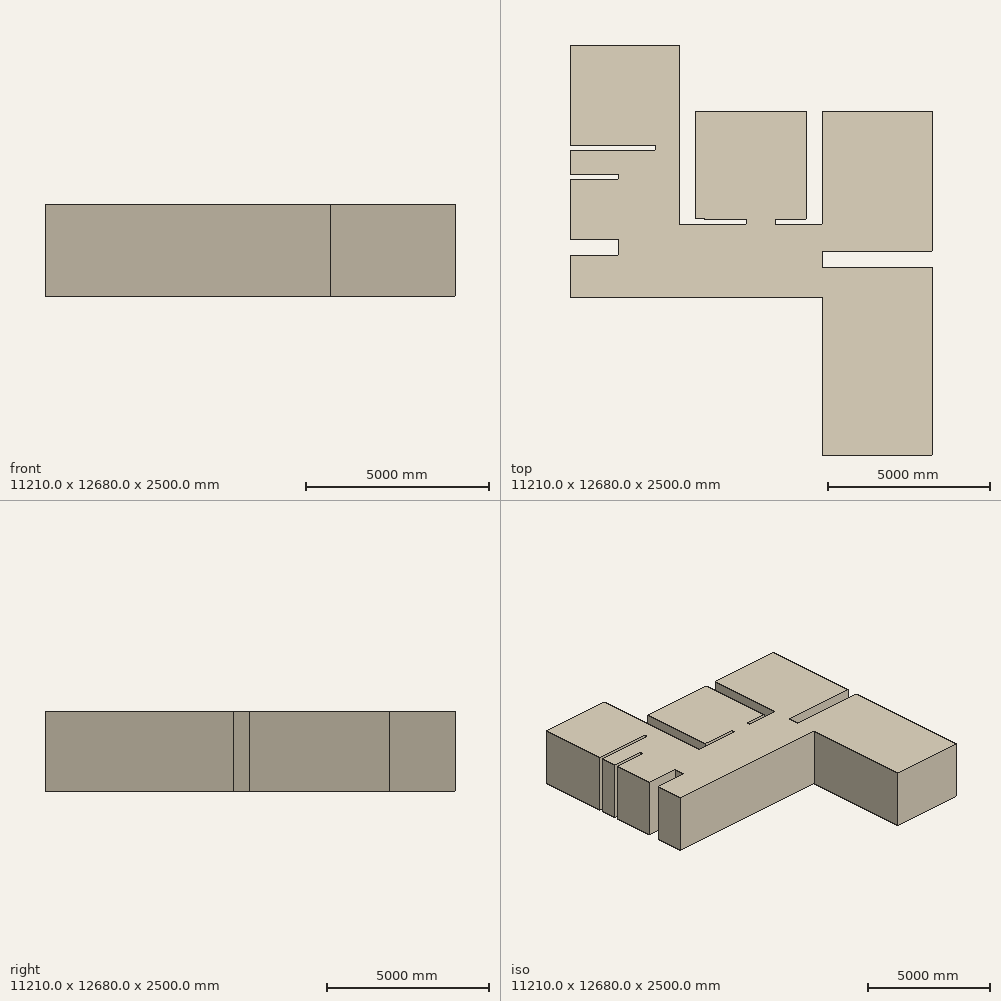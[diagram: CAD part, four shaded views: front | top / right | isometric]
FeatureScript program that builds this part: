
annotation { "Feature Type Name" : "Feature", "Feature Type Description" : "" }
export const myFeature = defineFeature(function(context is Context, id is Id, definition is map)
    precondition{}
    {
        {
            var Q0;
            Q0=qCreatedBy(makeId("Top.planeOp"),FACE);
            var sketch = newSketch(context, id + "F0", { "sketchPlane" : qUnion([Q0])});
            skLineSegment(sketch, "E0", {"start": v(0, 0) * mm, "end": v(-3380, 0) * mm});
            skLineSegment(sketch, "E1", {"start": v(-3380, 0) * mm, "end": v(-3380, -3100) * mm});
            skLineSegment(sketch, "E2", {"start": v(-3380, -3100) * mm, "end": v(-738.11, -3100) * mm});
            skLineSegment(sketch, "E3", {"start": v(-3380, -3980) * mm, "end": v(-1880, -3980) * mm});
            skLineSegment(sketch, "E4", {"start": v(-1880, -3980) * mm, "end": v(-1880, -4130) * mm});
            skLineSegment(sketch, "E5", {"start": v(-1880, -4130) * mm, "end": v(-3380, -4130) * mm});
            skLineSegment(sketch, "E6", {"start": v(-3380, -4130) * mm, "end": v(-3380, -6000) * mm});
            skLineSegment(sketch, "E7", {"start": v(-3380, -7790) * mm, "end": v(4420, -7790) * mm});
            skLineSegment(sketch, "E8", {"start": v(4420, -7790) * mm, "end": v(4420, -12680) * mm});
            skLineSegment(sketch, "E9", {"start": v(4420, -12680) * mm, "end": v(7830, -12680) * mm});
            skLineSegment(sketch, "E10", {"start": v(4420, -2030) * mm, "end": v(4420, -5380) * mm});
            skLineSegment(sketch, "E11", {"start": v(3920, -5380) * mm, "end": v(3920, -2030) * mm});
            skLineSegment(sketch, "E12", {"start": v(0, -2393) * mm, "end": v(0, 0) * mm});
            skLineSegment(sketch, "E13", {"start": v(500, -2030) * mm, "end": v(3920, -2030) * mm});
            skLineSegment(sketch, "E14", {"start": v(7830, -6370) * mm, "end": v(4420, -6370) * mm});
            skLineSegment(sketch, "E15", {"start": v(4420, -6370) * mm, "end": v(4420, -6870) * mm});
            skLineSegment(sketch, "E16", {"start": v(4420, -6870) * mm, "end": v(7830, -6870) * mm});
            skLineSegment(sketch, "E17", {"start": v(7830, -6870) * mm, "end": v(7830, -12680) * mm});
            skLineSegment(sketch, "E18", {"start": v(-738.11, -3100) * mm, "end": v(-738.11, -3250) * mm});
            skLineSegment(sketch, "E19", {"start": v(-738.11, -3250) * mm, "end": v(-3380, -3250) * mm});
            skLineSegment(sketch, "E20", {"start": v(-3380, -3250) * mm, "end": v(-3380, -3980) * mm});
            skLineSegment(sketch, "E21", {"start": v(-3380, -6000) * mm, "end": v(-1880, -6000) * mm});
            skLineSegment(sketch, "E22", {"start": v(-1880, -6000) * mm, "end": v(-1880, -6500) * mm});
            skLineSegment(sketch, "E23", {"start": v(-1880, -6500) * mm, "end": v(-3380, -6500) * mm});
            skLineSegment(sketch, "E24", {"start": v(-3380, -6500) * mm, "end": v(-3380, -7790) * mm});
            skLineSegment(sketch, "E25", {"start": v(0, -2393) * mm, "end": v(0, -5380) * mm});
            skLineSegment(sketch, "E26", {"start": v(4420, -2030) * mm, "end": v(7830, -2030) * mm});
            skLineSegment(sketch, "E27", {"start": v(7830, -2030) * mm, "end": v(7830, -6370) * mm});
            skLineSegment(sketch, "E28", {"start": v(0, -5380) * mm, "end": v(0, -5530) * mm});
            skLineSegment(sketch, "E29", {"start": v(0, -5530) * mm, "end": v(2066.42, -5530) * mm});
            skLineSegment(sketch, "E30", {"start": v(2066.42, -5530) * mm, "end": v(2055.7, -5380) * mm});
            skLineSegment(sketch, "E31", {"start": v(500, -2030) * mm, "end": v(500, -5362.31) * mm});
            skLineSegment(sketch, "E32", {"start": v(500, -5362.31) * mm, "end": v(2055.7, -5380) * mm});
            skLineSegment(sketch, "E33", {"start": v(3920, -5530) * mm, "end": v(2966.42, -5530) * mm});
            skLineSegment(sketch, "E34", {"start": v(2966.42, -5530) * mm, "end": v(2966.42, -5380) * mm});
            skLineSegment(sketch, "E35", {"start": v(3920, -5530) * mm, "end": v(4420, -5530) * mm});
            skLineSegment(sketch, "E36", {"start": v(4420, -5530) * mm, "end": v(4420, -5380) * mm});
            skLineSegment(sketch, "E37", {"start": v(2966.42, -5380) * mm, "end": v(3920, -5380) * mm});
            skLineSegment(sketch, "E38", {"start": v(500, -2030) * mm, "end": v(2210, -2030) * mm});
            skLineSegment(sketch, "E39", {"start": v(4420, -2030) * mm, "end": v(6125, -2030) * mm});
            skLineSegment(sketch, "E40", {"start": v(4420, -12680) * mm, "end": v(6125, -12680) * mm});
            skLineSegment(sketch, "E41", {"start": v(-3380, -5065) * mm, "end": v(-3380, -4130) * mm});
            skSolve(sketch);
        }
        {
            var Q0;
            Q0=makeQuery(id+"F0.imprint","IMPRINT",FACE,{"disambiguationData":[TD([[makeQuery(id+"F0.imprint","IMPRINT",EDGE,{"derivedFrom":sQuery(id+"F0.wireOp",EDGE,"E0")}),1.0]])]});
            extrude(context, id + "F1", {"entities" : qUnion([Q0]), "depth" : 2500 * mm, "offsetDistance" : 25 * mm});
        }
    });
